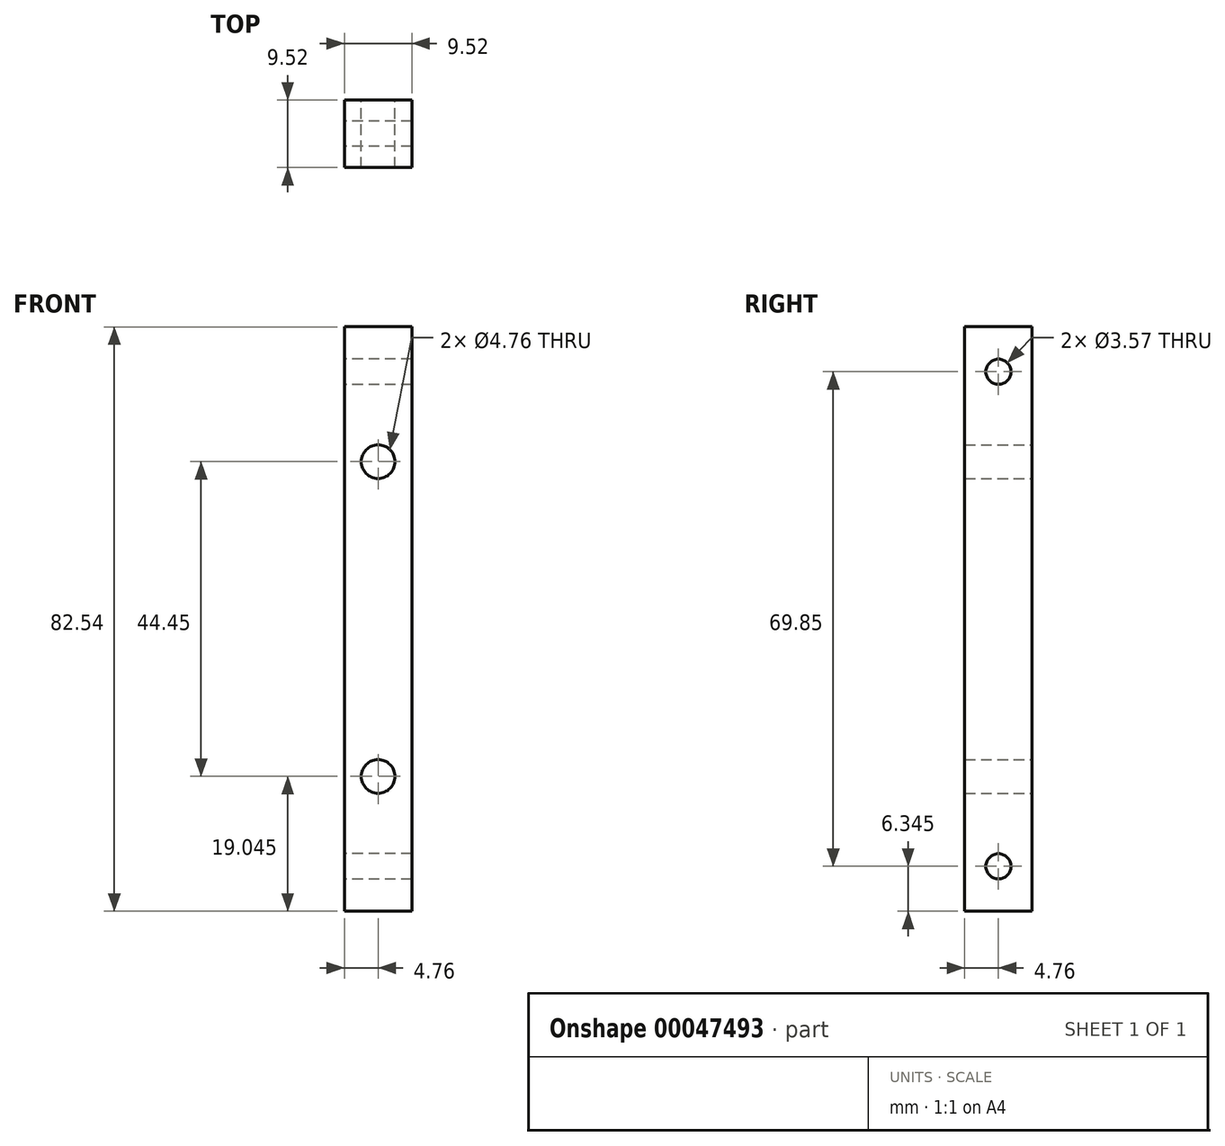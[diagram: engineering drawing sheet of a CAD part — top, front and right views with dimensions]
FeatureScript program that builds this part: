
annotation { "Feature Type Name" : "Feature", "Feature Type Description" : "" }
export const myFeature = defineFeature(function(context is Context, id is Id, definition is map)
    precondition{}
    {
        {
            var Q0;
            Q0=qCreatedBy(makeId("Top.planeOp"),FACE);
            var sketch = newSketch(context, id + "F0", { "sketchPlane" : qUnion([Q0])});
            skLineSegment(sketch, "E0.rect.bottom", {"start": v(4.76, 4.76) * mm, "end": v(-4.76, 4.76) * mm});
            skLineSegment(sketch, "E0.rect.top", {"start": v(4.76, -4.76) * mm, "end": v(-4.76, -4.76) * mm});
            skLineSegment(sketch, "E0.rect.left", {"start": v(4.76, 4.76) * mm, "end": v(4.76, -4.76) * mm});
            skLineSegment(sketch, "E0.rect.right", {"start": v(-4.76, 4.76) * mm, "end": v(-4.76, -4.76) * mm});
            skPoint(sketch, "E0.rect.middle", {"position": v(0, 0) * mm});
            skSolve(sketch);
        }
        {
            var Q0;
            Q0 = qSketchRegion(id + "F0", true);
            extrude(context, id + "F1", {"entities" : qUnion([Q0]), "depth" : 82.55 * mm, "symmetric" : true});
        }
        {
            var Q0;
            Q0=makeQuery(id+"F1.opExtrude","SWEPT_FACE",FACE,{"disambiguationData":[OSD([sQuery(id+"F0.wireOp",EDGE,"E0.rect.right")])]});
            var sketch = newSketch(context, id + "F2", { "sketchPlane" : qUnion([Q0])});
            skCircle(sketch, "E1", {"center": v(0, 34.93) * mm, "radius": 1.79 * mm});
            skCircle(sketch, "E2.MirrorC", {"center": v(0, -34.93) * mm, "radius": 1.79 * mm});
            skSolve(sketch);
        }
        {
            var Q0;
            Q0 = qSketchRegion(id + "F2", true);
            var Q1;
            Q1=makeQuery(id+"F1.opExtrude","SWEPT_FACE",FACE,{"disambiguationData":[OSD([sQuery(id+"F0.wireOp",EDGE,"E0.rect.left")])]});
            extrude(context, id + "F3", {"entities" : qUnion([Q0]), "operationType" : NewBodyOperationType.REMOVE, "endBound" : BoundingType.UP_TO_SURFACE, "oppositeDirection" : true, "endBoundEntityFace" : qUnion([Q1]), "depth" : 25.4 * mm});
        }
        {
            var Q0;
            Q0=makeQuery(id+"F1.opExtrude","SWEPT_FACE",FACE,{"disambiguationData":[OSD([sQuery(id+"F0.wireOp",EDGE,"E0.rect.bottom")])]});
            var sketch = newSketch(context, id + "F4", { "sketchPlane" : qUnion([Q0])});
            skCircle(sketch, "E3", {"center": v(0, -22.23) * mm, "radius": 2.38 * mm});
            skCircle(sketch, "E4.MirrorC", {"center": v(0, 22.23) * mm, "radius": 2.38 * mm});
            skSolve(sketch);
        }
        {
            var Q0;
            Q0 = qSketchRegion(id + "F4", true);
            var Q1;
            Q1=makeQuery(id+"F1.opExtrude","SWEPT_FACE",FACE,{"disambiguationData":[OSD([sQuery(id+"F0.wireOp",EDGE,"E0.rect.top")])]});
            extrude(context, id + "F5", {"entities" : qUnion([Q0]), "operationType" : NewBodyOperationType.REMOVE, "endBound" : BoundingType.UP_TO_SURFACE, "oppositeDirection" : true, "endBoundEntityFace" : qUnion([Q1]), "depth" : 25.4 * mm});
        }
    });
